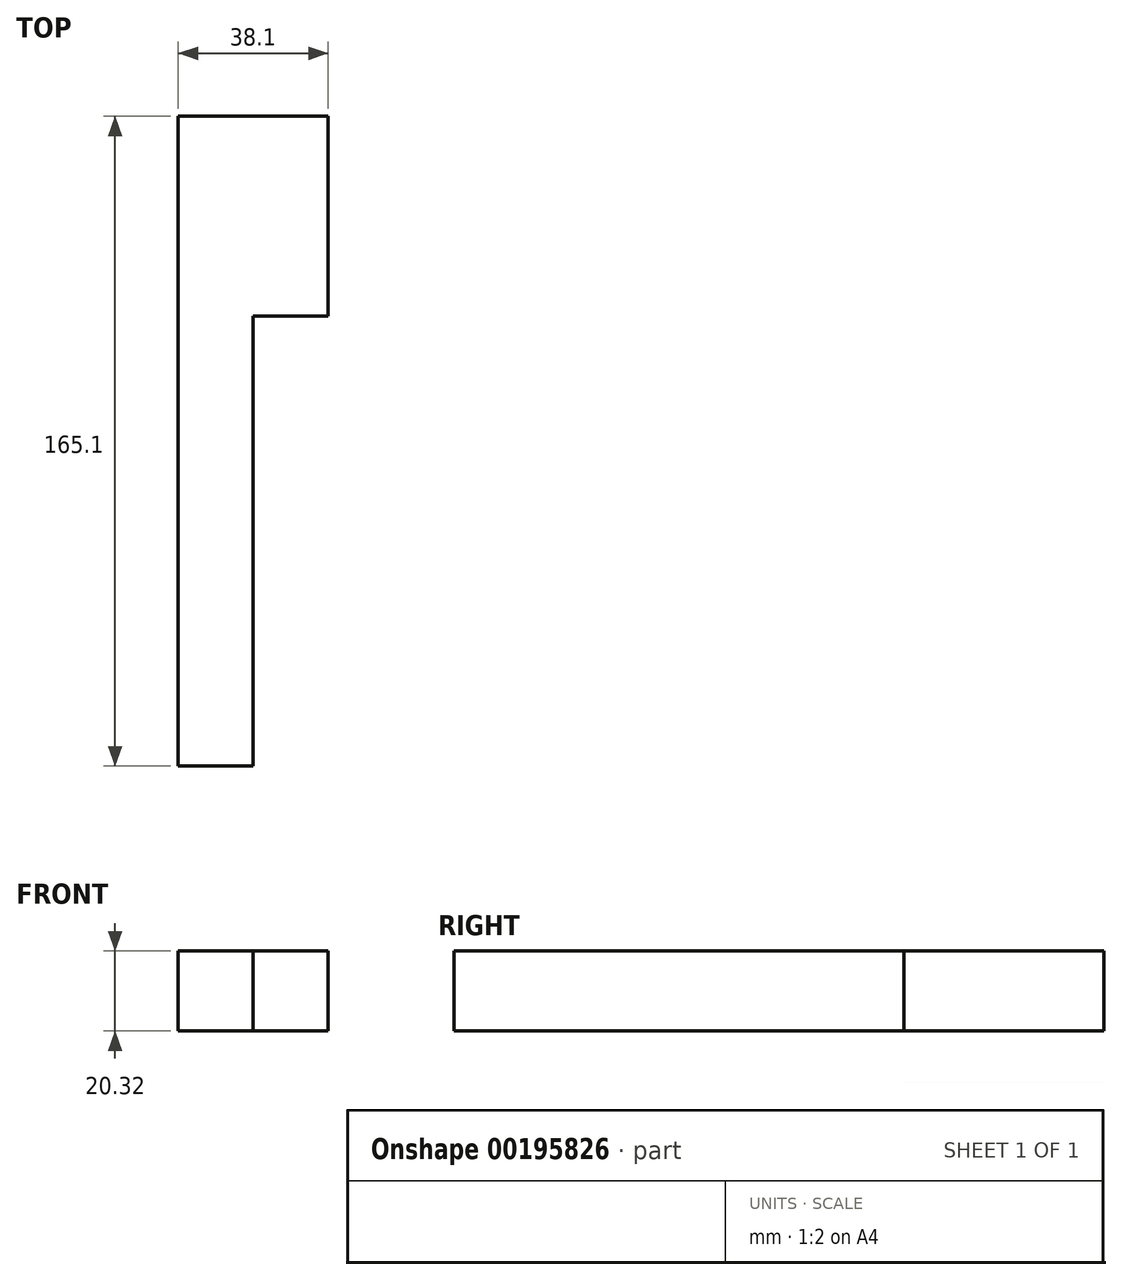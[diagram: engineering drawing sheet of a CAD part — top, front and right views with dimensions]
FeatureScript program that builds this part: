
annotation { "Feature Type Name" : "Feature", "Feature Type Description" : "" }
export const myFeature = defineFeature(function(context is Context, id is Id, definition is map)
    precondition{}
    {
        {
            var Q0;
            Q0=qCreatedBy(makeId("Top.planeOp"),FACE);
            var sketch = newSketch(context, id + "F0", { "sketchPlane" : qUnion([Q0])});
            skLineSegment(sketch, "E0.bottom", {"start": v(-19.05, 82.55) * mm, "end": v(19.05, 82.55) * mm});
            skLineSegment(sketch, "E0.top", {"start": v(-19.05, -82.55) * mm, "end": v(19.05, -82.55) * mm});
            skLineSegment(sketch, "E0.left", {"start": v(-19.05, 82.55) * mm, "end": v(-19.05, -82.55) * mm});
            skLineSegment(sketch, "E0.right", {"start": v(19.05, 82.55) * mm, "end": v(19.05, -82.55) * mm});
            skPoint(sketch, "E0.middle", {"position": v(0, 0) * mm});
            skLineSegment(sketch, "E1", {"start": v(0, 31.75) * mm, "end": v(0, -82.55) * mm});
            skPoint(sketch, "E1.endSnap0", {"position": v(0, -82.55) * mm});
            skLineSegment(sketch, "E2", {"start": v(0, 31.75) * mm, "end": v(19.05, 31.75) * mm});
            skSolve(sketch);
        }
        {
            var Q0;
            {var subQ1=sQuery(id+"F0.wireOp",EDGE,"E0.bottom");Q0=makeQuery(id+"F0.imprint","IMPRINT",FACE,{"disambiguationData":[TD([[makeQuery(id+"F0.imprint","IMPRINT",EDGE,{"derivedFrom":subQ1}),-1.0]])]});}
            extrude(context, id + "F1", {"entities" : qUnion([Q0]), "depth" : 20.32 * mm});
        }
    });
